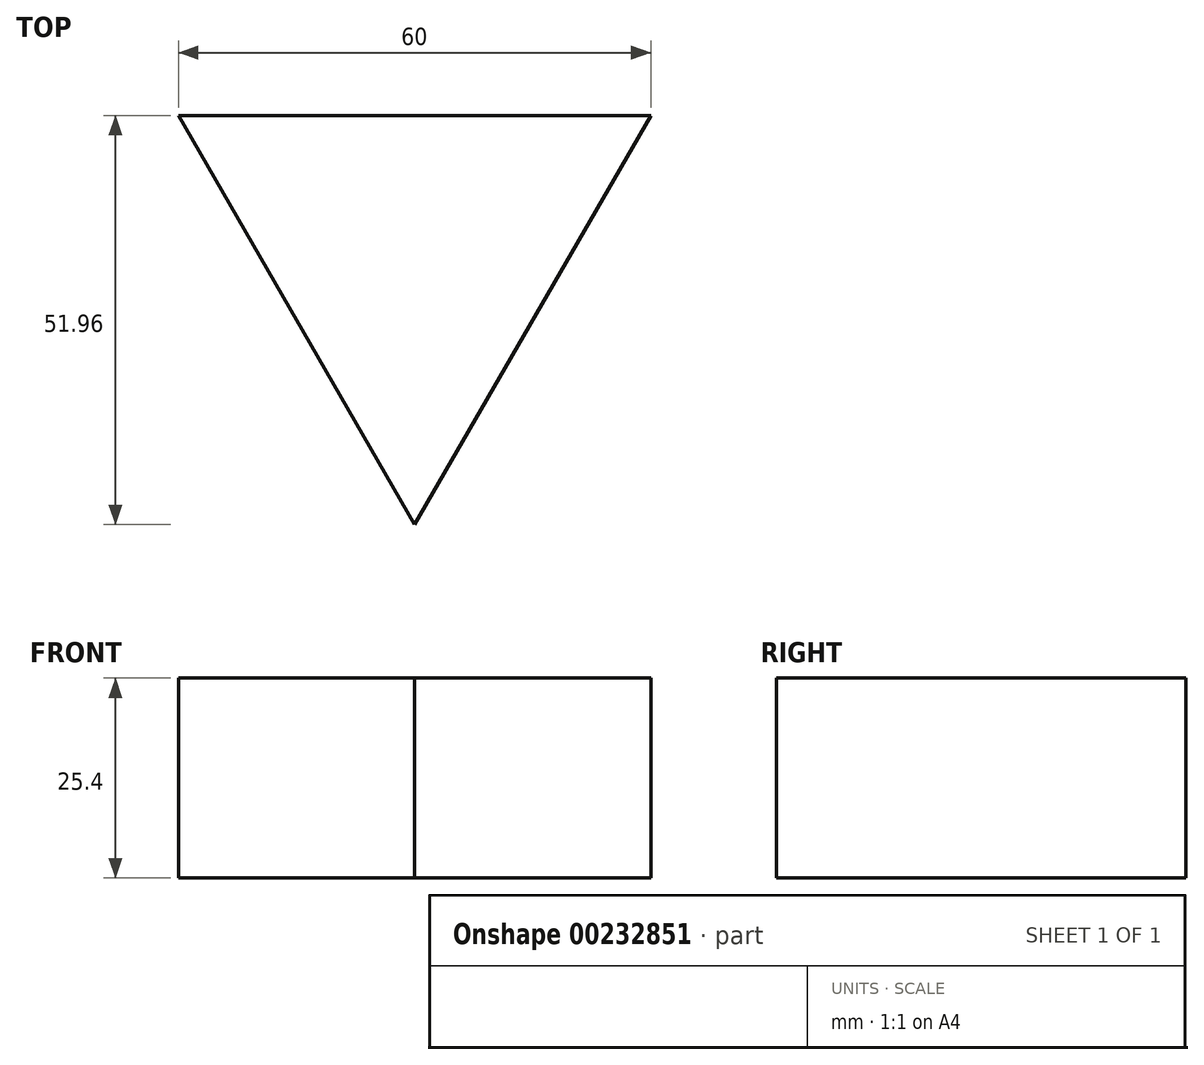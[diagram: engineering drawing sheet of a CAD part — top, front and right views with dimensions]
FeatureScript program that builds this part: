
annotation { "Feature Type Name" : "Feature", "Feature Type Description" : "" }
export const myFeature = defineFeature(function(context is Context, id is Id, definition is map)
    precondition{}
    {
        {
            var Q0;
            Q0=qCreatedBy(makeId("Top.planeOp"),FACE);
            var sketch = newSketch(context, id + "F0", { "sketchPlane" : qUnion([Q0])});
            skLineSegment(sketch, "E0", {"start": v(-72.05, 56.24) * mm, "end": v(-12.05, 56.24) * mm});
            skLineSegment(sketch, "E1", {"start": v(-12.05, 56.24) * mm, "end": v(-42.05, 4.28) * mm});
            skLineSegment(sketch, "E2", {"start": v(-42.05, 4.28) * mm, "end": v(-72.05, 56.24) * mm});
            skLineSegment(sketch, "E3", {"start": v(5.5, 5.31) * mm, "end": v(105.5, 5.31) * mm});
            skLineSegment(sketch, "E4", {"start": v(25.5, 51.14) * mm, "end": v(85.5, 51.14) * mm});
            skLineSegment(sketch, "E5", {"start": v(85.5, 51.14) * mm, "end": v(105.5, 5.31) * mm});
            skLineSegment(sketch, "E6", {"start": v(25.5, 51.14) * mm, "end": v(5.5, 5.31) * mm});
            skLineSegment(sketch, "E7", {"start": v(131.94, -25.48) * mm, "end": v(103.54, -74.67) * mm});
            skLineSegment(sketch, "E8", {"start": v(103.54, -74.67) * mm, "end": v(23.54, -74.67) * mm});
            skLineSegment(sketch, "E9", {"start": v(23.54, -74.67) * mm, "end": v(47.48, -8.9) * mm});
            skLineSegment(sketch, "E10", {"start": v(47.48, -8.9) * mm, "end": v(72.65, -21.17) * mm});
            skLineSegment(sketch, "E11", {"start": v(47.48, -8.9) * mm, "end": v(93.53, -8.9) * mm});
            skSolve(sketch);
        }
        {
            var Q0;
            Q0=makeQuery(id+"F0.imprint","IMPRINT",FACE,{"disambiguationData":[TD([[makeQuery(id+"F0.imprint","IMPRINT",EDGE,{"derivedFrom":sQuery(id+"F0.wireOp",EDGE,"E0")}),-1.0]])]});
            extrude(context, id + "F1", {"entities" : qUnion([Q0]), "depth" : 25.4 * mm});
        }
    });
